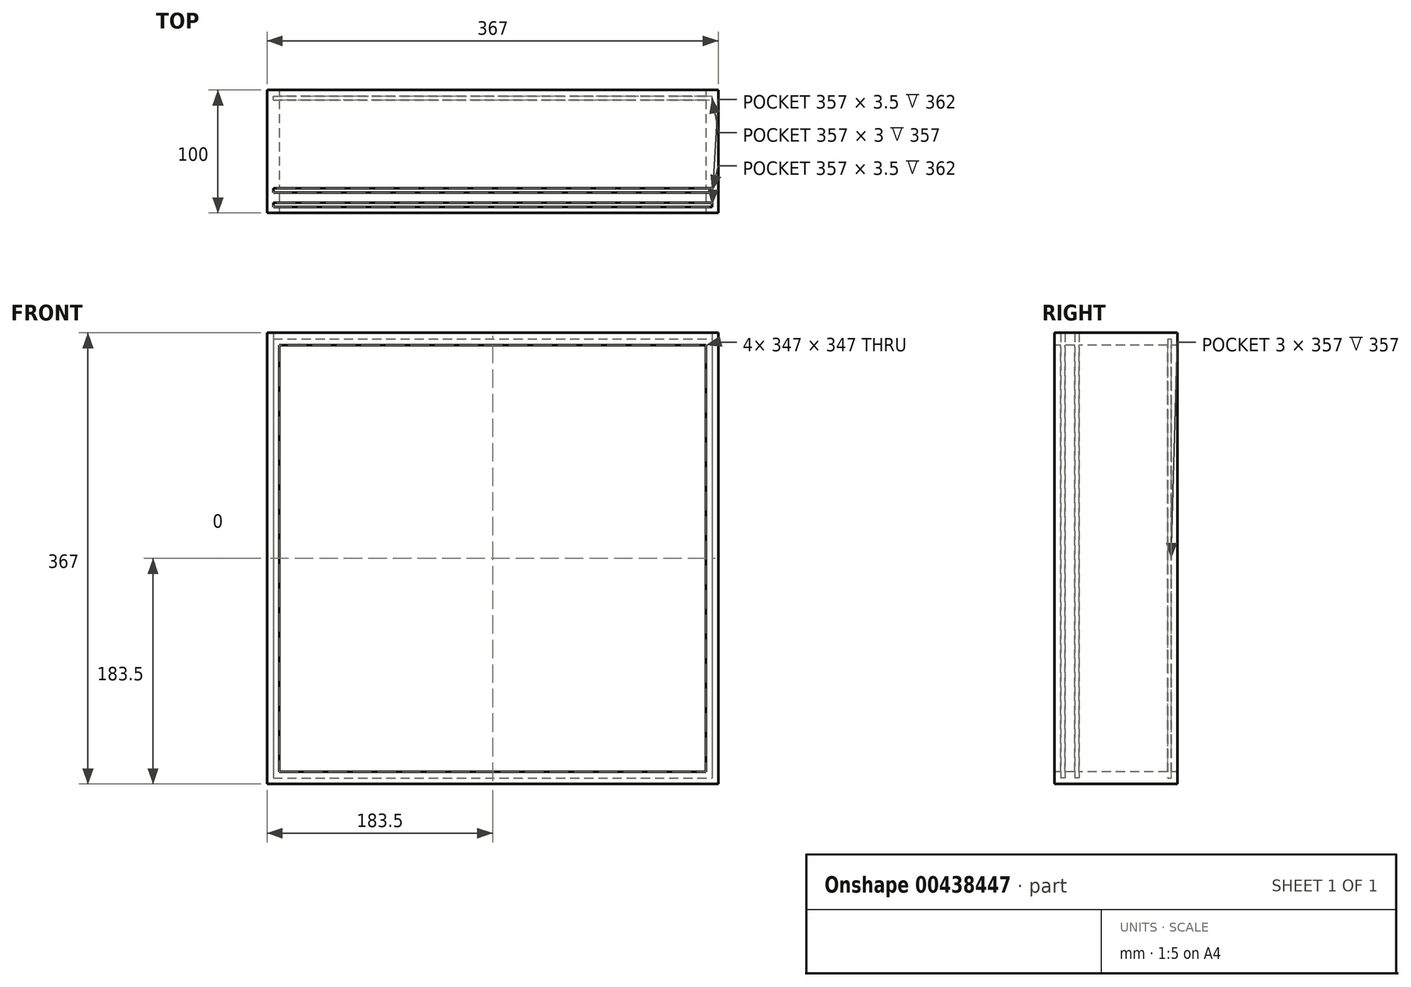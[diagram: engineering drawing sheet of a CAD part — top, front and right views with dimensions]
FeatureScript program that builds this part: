
annotation { "Feature Type Name" : "Feature", "Feature Type Description" : "" }
export const myFeature = defineFeature(function(context is Context, id is Id, definition is map)
    precondition{}
    {
        {
            var Q0;
            Q0=qCreatedBy(makeId("Front.planeOp"),FACE);
            var sketch = newSketch(context, id + "F0", { "sketchPlane" : qUnion([Q0])});
            skLineSegment(sketch, "E0.bottom", {"start": v(-177.8, 177.8) * mm, "end": v(177.8, 177.8) * mm});
            skLineSegment(sketch, "E0.top", {"start": v(-177.8, -177.8) * mm, "end": v(177.8, -177.8) * mm});
            skLineSegment(sketch, "E0.left", {"start": v(-177.8, 177.8) * mm, "end": v(-177.8, -177.8) * mm});
            skLineSegment(sketch, "E0.right", {"start": v(177.8, 177.8) * mm, "end": v(177.8, -177.8) * mm});
            skSolve(sketch);
        }
        {
            var Q0;
            Q0=qCreatedBy(makeId("Front.planeOp"),FACE);
            var sketch = newSketch(context, id + "F1", { "sketchPlane" : qUnion([Q0])});
            skLineSegment(sketch, "E1.0", {"start": v(-183.5, 183.5) * mm, "end": v(183.5, 183.5) * mm});
            skLineSegment(sketch, "E1.1", {"start": v(-183.5, 183.5) * mm, "end": v(-183.5, -183.5) * mm});
            skLineSegment(sketch, "E1.2", {"start": v(-183.5, -183.5) * mm, "end": v(183.5, -183.5) * mm});
            skLineSegment(sketch, "E1.3", {"start": v(183.5, 183.5) * mm, "end": v(183.5, -183.5) * mm});
            skSolve(sketch);
        }
        {
            var Q0;
            Q0=makeQuery(id+"F1.imprint","IMPRINT",FACE,{"disambiguationData":[TD([[makeQuery(id+"F1.imprint","IMPRINT",EDGE,{"derivedFrom":sQuery(id+"F1.wireOp",EDGE,"E1.0")}),-1.0]])]});
            extrude(context, id + "F2", {"entities" : qUnion([Q0]), "oppositeDirection" : true, "depth" : 100 * mm});
        }
        {
            var Q0;
            Q0=qCreatedBy(makeId("Front.planeOp"),FACE);
            var sketch = newSketch(context, id + "F3", { "sketchPlane" : qUnion([Q0])});
            skLineSegment(sketch, "E2.0", {"start": v(-173.5, 173.5) * mm, "end": v(173.5, 173.5) * mm});
            skLineSegment(sketch, "E2.1", {"start": v(-173.5, 173.5) * mm, "end": v(-173.5, -173.5) * mm});
            skLineSegment(sketch, "E2.2", {"start": v(-173.5, -173.5) * mm, "end": v(173.5, -173.5) * mm});
            skLineSegment(sketch, "E2.3", {"start": v(173.5, 173.5) * mm, "end": v(173.5, -173.5) * mm});
            skSolve(sketch);
        }
        {
            var Q0;
            Q0=makeQuery(id+"F3.imprint","IMPRINT",FACE,{"disambiguationData":[TD([[makeQuery(id+"F3.imprint","IMPRINT",EDGE,{"derivedFrom":sQuery(id+"F3.wireOp",EDGE,"E2.0")}),-1.0]])]});
            extrude(context, id + "F4", {"entities" : qUnion([Q0]), "operationType" : NewBodyOperationType.REMOVE, "endBound" : BoundingType.THROUGH_ALL, "oppositeDirection" : true, "depth" : 25 * mm});
        }
        {
            var Q0;
            Q0=qCreatedBy(makeId("Front.planeOp"),FACE);
            cPlane(context, id + "F5", {"entities" : qUnion([Q0]), "cplaneType" : CPlaneType.OFFSET, "offset" : 5 * mm, "oppositeDirection" : true, "width" : 150 * mm, "height" : 150 * mm});
        }
        {
            var Q0;
            Q0=qCreatedBy(id+"F5.planeOp",FACE);
            var sketch = newSketch(context, id + "F6", { "sketchPlane" : qUnion([Q0])});
            skLineSegment(sketch, "E3.1", {"start": v(-178.5, 183.5) * mm, "end": v(-178.5, -178.5) * mm});
            skLineSegment(sketch, "E3.2", {"start": v(-178.5, -178.5) * mm, "end": v(178.5, -178.5) * mm});
            skLineSegment(sketch, "E3.3", {"start": v(178.5, 183.5) * mm, "end": v(178.5, -178.5) * mm});
            skLineSegment(sketch, "E4", {"start": v(-178.5, 183.5) * mm, "end": v(178.5, 183.5) * mm});
            skSolve(sketch);
        }
        {
            var Q0;
            Q0 = qSketchRegion(id + "F6", true);
            extrude(context, id + "F7", {"entities" : qUnion([Q0]), "operationType" : NewBodyOperationType.REMOVE, "oppositeDirection" : true, "depth" : 3.5 * mm});
        }
        {
            var Q0;
            Q0=qCreatedBy(makeId("Front.planeOp"),FACE);
            cPlane(context, id + "F8", {"entities" : qUnion([Q0]), "cplaneType" : CPlaneType.OFFSET, "offset" : 95 * mm, "oppositeDirection" : true, "width" : 150 * mm, "height" : 150 * mm});
        }
        {
            var Q0;
            Q0=qCreatedBy(id+"F8.planeOp",FACE);
            var sketch = newSketch(context, id + "F9", { "sketchPlane" : qUnion([Q0])});
            skLineSegment(sketch, "E5.0", {"start": v(-178.5, 178.5) * mm, "end": v(-178.5, -178.5) * mm});
            skLineSegment(sketch, "E6.0", {"start": v(178.5, 178.5) * mm, "end": v(178.5, -178.5) * mm});
            skLineSegment(sketch, "E7.0", {"start": v(-178.5, -178.5) * mm, "end": v(178.5, -178.5) * mm});
            skLineSegment(sketch, "E8", {"start": v(-178.5, 178.5) * mm, "end": v(178.5, 178.5) * mm});
            skPoint(sketch, "E9.orphan", {"position": v(-178.5, 183.5) * mm});
            skPoint(sketch, "E10.orphan", {"position": v(178.5, 183.5) * mm});
            skSolve(sketch);
        }
        {
            var Q0;
            Q0 = qSketchRegion(id + "F9", true);
            extrude(context, id + "F10", {"entities" : qUnion([Q0]), "operationType" : NewBodyOperationType.REMOVE, "depth" : 3 * mm});
        }
        {
            var Q0;
            Q0=qCreatedBy(makeId("Front.planeOp"),FACE);
            cPlane(context, id + "F11", {"entities" : qUnion([Q0]), "cplaneType" : CPlaneType.OFFSET, "offset" : 16.5 * mm, "oppositeDirection" : true, "width" : 150 * mm, "height" : 150 * mm});
        }
        {
            var Q0;
            Q0=qCreatedBy(id+"F11.planeOp",FACE);
            var sketch = newSketch(context, id + "F12", { "sketchPlane" : qUnion([Q0])});
            skLineSegment(sketch, "E11.0", {"start": v(-178.5, 183.5) * mm, "end": v(-178.5, -178.5) * mm});
            skLineSegment(sketch, "E12.0", {"start": v(-178.5, 183.5) * mm, "end": v(178.5, 183.5) * mm});
            skLineSegment(sketch, "E13.0", {"start": v(178.5, 183.5) * mm, "end": v(178.5, -178.5) * mm});
            skLineSegment(sketch, "E14.0", {"start": v(-178.5, -178.5) * mm, "end": v(178.5, -178.5) * mm});
            skSolve(sketch);
        }
        {
            var Q0;
            Q0 = qSketchRegion(id + "F12", true);
            extrude(context, id + "F13", {"entities" : qUnion([Q0]), "operationType" : NewBodyOperationType.REMOVE, "oppositeDirection" : true, "depth" : 3.5 * mm});
        }
    });
